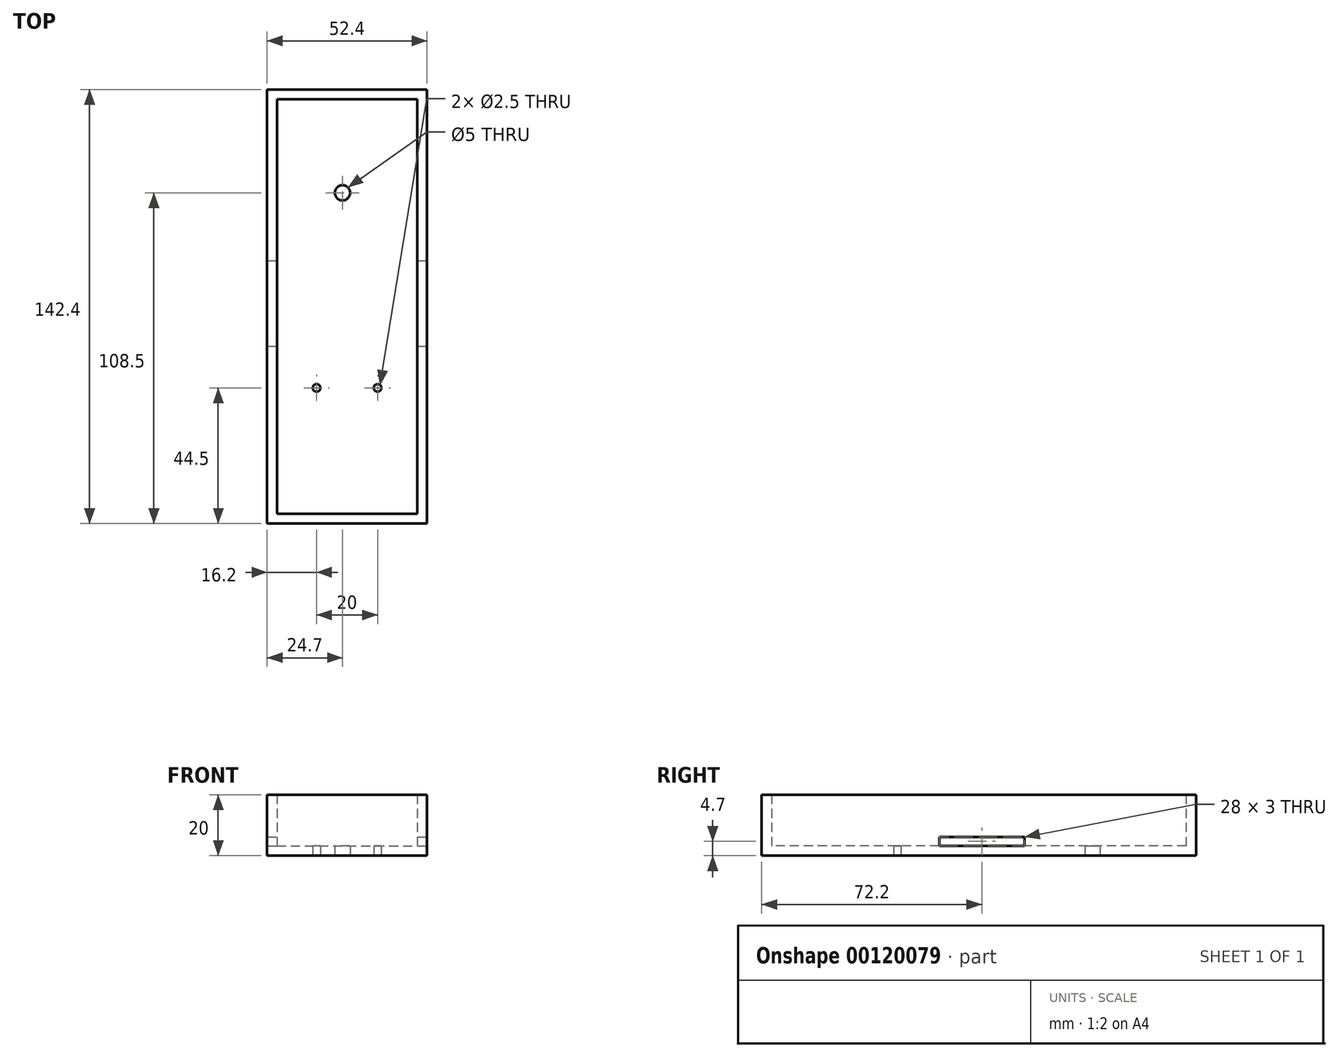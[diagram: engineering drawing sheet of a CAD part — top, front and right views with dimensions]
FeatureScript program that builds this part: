
annotation { "Feature Type Name" : "Feature", "Feature Type Description" : "" }
export const myFeature = defineFeature(function(context is Context, id is Id, definition is map)
    precondition{}
    {
        {
            var Q0;
            Q0=qCreatedBy(makeId("Top.planeOp"),FACE);
            var sketch = newSketch(context, id + "F0", { "sketchPlane" : qUnion([Q0])});
            skLineSegment(sketch, "E0.bottom", {"start": v(23, -68) * mm, "end": v(-23, -68) * mm});
            skLineSegment(sketch, "E0.top", {"start": v(23, 68) * mm, "end": v(-23, 68) * mm});
            skLineSegment(sketch, "E0.left", {"start": v(23, -68) * mm, "end": v(23, 68) * mm});
            skLineSegment(sketch, "E0.right", {"start": v(-23, -68) * mm, "end": v(-23, 68) * mm});
            skPoint(sketch, "E0.middle", {"position": v(0, 0) * mm});
            skLineSegment(sketch, "E1.0", {"start": v(26.2, -71.2) * mm, "end": v(-26.2, -71.2) * mm});
            skLineSegment(sketch, "E1.1", {"start": v(26.2, -71.2) * mm, "end": v(26.2, 71.2) * mm});
            skLineSegment(sketch, "E1.2", {"start": v(26.2, 71.2) * mm, "end": v(-26.2, 71.2) * mm});
            skLineSegment(sketch, "E1.3", {"start": v(-26.2, -71.2) * mm, "end": v(-26.2, 71.2) * mm});
            skLineSegment(sketch, "E2", {"start": v(0, -71.2) * mm, "end": v(0, 71.2) * mm, "construction": true});
            skLineSegment(sketch, "E3", {"start": v(-26.2, -26.7) * mm, "end": v(26.2, -26.7) * mm, "construction": true});
            skLineSegment(sketch, "E4", {"start": v(10, -26.7) * mm, "end": v(10, -71.2) * mm, "construction": true});
            skCircle(sketch, "E5", {"center": v(10, -26.7) * mm, "radius": 1.25 * mm});
            skCircle(sketch, "E6.MirrorC", {"center": v(-10, -26.7) * mm, "radius": 1.25 * mm});
            skLineSegment(sketch, "E7", {"start": v(-23, 37.3) * mm, "end": v(23, 37.3) * mm, "construction": true});
            skCircle(sketch, "E8", {"center": v(-1.5, 37.3) * mm, "radius": 2.5 * mm});
            skSolve(sketch);
        }
        {
            var Q0;
            Q0=makeQuery(id+"F0.imprint","IMPRINT",FACE,{"disambiguationData":[TD([[makeQuery(id+"F0.imprint","IMPRINT",EDGE,{"derivedFrom":sQuery(id+"F0.wireOp",EDGE,"E0.bottom")}),1.0]])]});
            var Q1;
            Q1=makeQuery(id+"F0.imprint","IMPRINT",FACE,{"disambiguationData":[TD([[makeQuery(id+"F0.imprint","IMPRINT",EDGE,{"derivedFrom":sQuery(id+"F0.wireOp",EDGE,"E0.bottom")}),-1.0]])]});
            extrude(context, id + "F1", {"entities" : qUnion([Q0, Q1]), "depth" : 3.2 * mm});
        }
        {
            var Q0;
            Q0=makeQuery(id+"F0.imprint","IMPRINT",FACE,{"disambiguationData":[TD([[makeQuery(id+"F0.imprint","IMPRINT",EDGE,{"derivedFrom":sQuery(id+"F0.wireOp",EDGE,"E0.bottom")}),1.0]])]});
            extrude(context, id + "F2", {"entities" : qUnion([Q0]), "operationType" : NewBodyOperationType.ADD, "depth" : 20 * mm});
        }
        {
            var Q0;
            Q0=makeQuery(id+"F2.opExtrude","SWEPT_FACE",FACE,{"disambiguationData":[OSD([sQuery(id+"F0.wireOp",EDGE,"E0.right")])]});
            var sketch = newSketch(context, id + "F3", { "sketchPlane" : qUnion([Q0])});
            skLineSegment(sketch, "E9.bottom", {"start": v(-13, 3.2) * mm, "end": v(15, 3.2) * mm});
            skLineSegment(sketch, "E9.top", {"start": v(-13, 6.2) * mm, "end": v(15, 6.2) * mm});
            skLineSegment(sketch, "E9.left", {"start": v(-13, 3.2) * mm, "end": v(-13, 6.2) * mm});
            skLineSegment(sketch, "E9.right", {"start": v(15, 3.2) * mm, "end": v(15, 6.2) * mm});
            skSolve(sketch);
        }
        {
            var Q0;
            Q0=makeQuery(id+"F3.imprint","IMPRINT",FACE,{"disambiguationData":[TD([[makeQuery(id+"F3.imprint","IMPRINT",EDGE,{"derivedFrom":sQuery(id+"F3.wireOp",EDGE,"E9.bottom")}),-1.0]])]});
            extrude(context, id + "F4", {"entities" : qUnion([Q0]), "operationType" : NewBodyOperationType.REMOVE, "endBound" : BoundingType.THROUGH_ALL, "oppositeDirection" : true, "depth" : 25 * mm, "hasSecondDirection" : true, "secondDirectionBound" : SecondDirectionBoundingType.THROUGH_ALL, "secondDirectionOppositeDirection" : false, "secondDirectionDepth" : 25 * mm});
        }
    });
